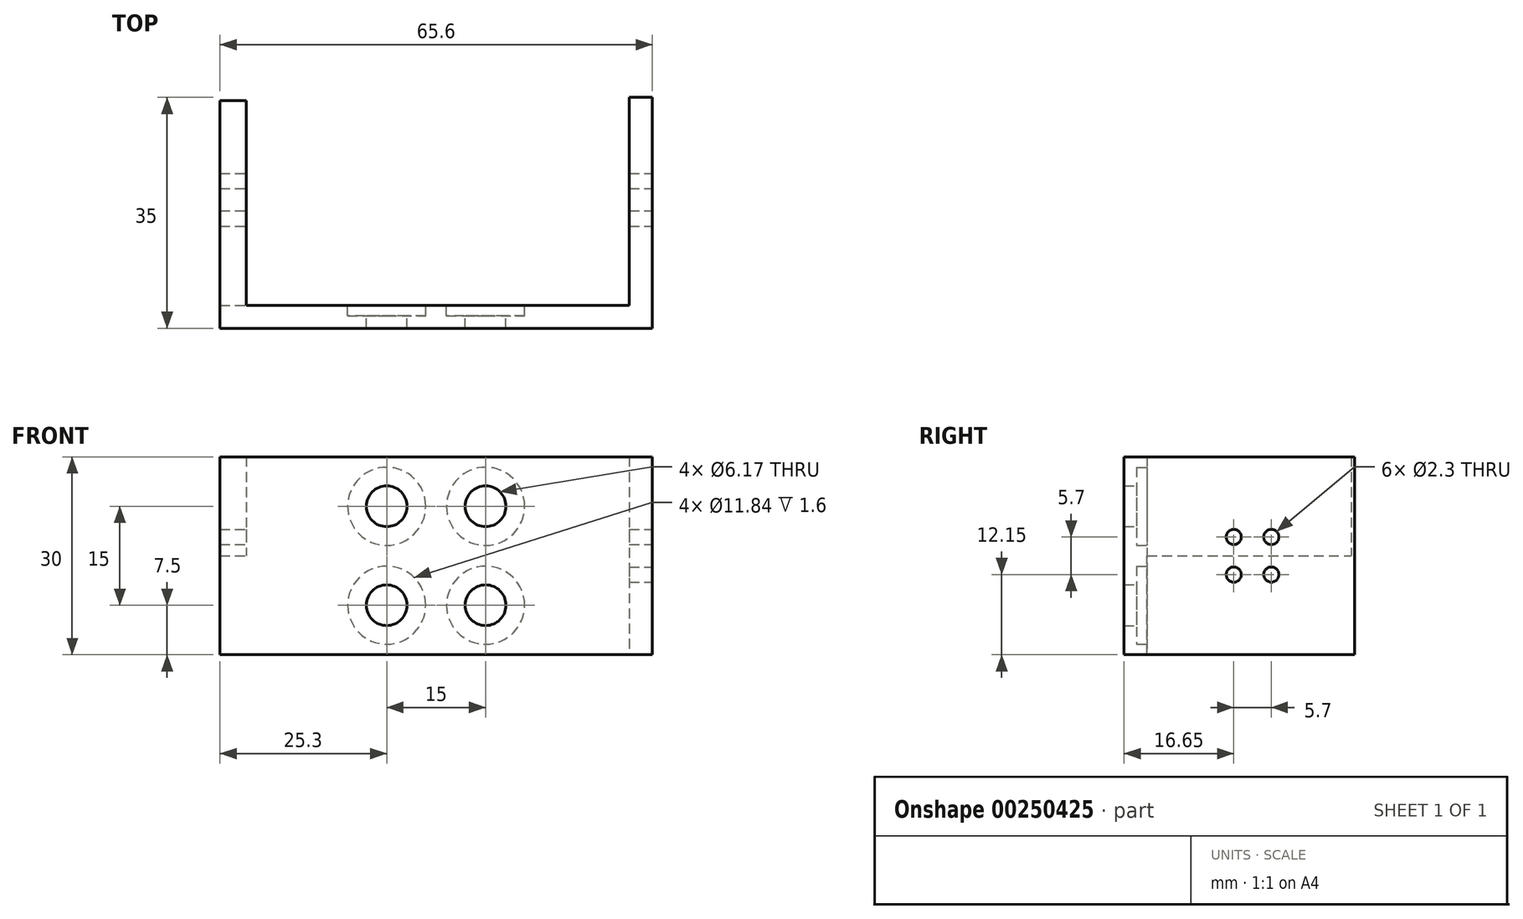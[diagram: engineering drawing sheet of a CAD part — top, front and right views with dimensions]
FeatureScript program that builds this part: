
annotation { "Feature Type Name" : "Feature", "Feature Type Description" : "" }
export const myFeature = defineFeature(function(context is Context, id is Id, definition is map)
    precondition{}
    {
        {
            var Q0;
            Q0=qCreatedBy(makeId("Front.planeOp"),FACE);
            var sketch = newSketch(context, id + "F0", { "sketchPlane" : qUnion([Q0])});
            skLineSegment(sketch, "E0.bottom", {"start": v(32.8, -15) * mm, "end": v(-32.8, -15) * mm});
            skLineSegment(sketch, "E0.top", {"start": v(32.8, 15) * mm, "end": v(-32.8, 15) * mm});
            skLineSegment(sketch, "E0.left", {"start": v(32.8, -15) * mm, "end": v(32.8, 15) * mm});
            skLineSegment(sketch, "E0.right", {"start": v(-32.8, -15) * mm, "end": v(-32.8, 15) * mm});
            skPoint(sketch, "E0.middle", {"position": v(0, 0) * mm});
            skSolve(sketch);
        }
        {
            var Q0;
            Q0 = qSketchRegion(id + "F0", true);
            extrude(context, id + "F1", {"entities" : qUnion([Q0]), "endBound" : BoundingType.SYMMETRIC, "depth" : 3.5 * mm});
        }
        {
            var Q0;
            Q0=qCreatedBy(makeId("Top.planeOp"),FACE);
            var sketch = newSketch(context, id + "F2", { "sketchPlane" : qUnion([Q0])});
            skLineSegment(sketch, "E1.bottom", {"start": v(32.8, 1.75) * mm, "end": v(29.3, 1.75) * mm});
            skLineSegment(sketch, "E1.top", {"start": v(32.8, 33.25) * mm, "end": v(29.3, 33.25) * mm});
            skLineSegment(sketch, "E1.left", {"start": v(32.8, 1.75) * mm, "end": v(32.8, 33.25) * mm});
            skLineSegment(sketch, "E1.right", {"start": v(29.3, 1.75) * mm, "end": v(29.3, 33.25) * mm});
            skSolve(sketch);
        }
        {
            var Q0;
            Q0 = qSketchRegion(id + "F2", true);
            extrude(context, id + "F3", {"entities" : qUnion([Q0]), "operationType" : NewBodyOperationType.ADD, "endBound" : BoundingType.SYMMETRIC, "depth" : 30 * mm});
        }
        {
            var Q0;
            Q0=qCreatedBy(makeId("Top.planeOp"),FACE);
            var sketch = newSketch(context, id + "F4", { "sketchPlane" : qUnion([Q0])});
            skLineSegment(sketch, "E2.bottom", {"start": v(-32.8, 1.75) * mm, "end": v(-28.8, 1.75) * mm});
            skLineSegment(sketch, "E2.top", {"start": v(-32.8, 32.75) * mm, "end": v(-28.8, 32.75) * mm});
            skLineSegment(sketch, "E2.left", {"start": v(-32.8, 1.75) * mm, "end": v(-32.8, 32.75) * mm});
            skLineSegment(sketch, "E2.right", {"start": v(-28.8, 1.75) * mm, "end": v(-28.8, 32.75) * mm});
            skSolve(sketch);
        }
        {
            var Q0;
            Q0 = qSketchRegion(id + "F4", true);
            extrude(context, id + "F5", {"entities" : qUnion([Q0]), "operationType" : NewBodyOperationType.ADD, "depth" : 15 * mm});
        }
        {
            var Q0;
            Q0=makeQuery(id+"F3.boolean.opBoolean","MERGE",FACE,{"derivedFrom":[makeQuery(id+"F1.opExtrude","SWEPT_FACE",FACE,{"disambiguationData":[OSD([sQuery(id+"F0.wireOp",EDGE,"E0.left")])]}),makeQuery(id+"F3.opExtrude","SWEPT_FACE",FACE,{"disambiguationData":[OSD([sQuery(id+"F2.wireOp",EDGE,"E1.left")])]})]});
            var sketch = newSketch(context, id + "F6", { "sketchPlane" : qUnion([Q0])});
            skCircle(sketch, "E3", {"center": v(14.9, 2.85) * mm, "radius": 1.15 * mm});
            skCircle(sketch, "E4", {"center": v(20.6, 2.85) * mm, "radius": 1.15 * mm});
            skCircle(sketch, "E5", {"center": v(14.9, -2.85) * mm, "radius": 1.15 * mm});
            skCircle(sketch, "E6", {"center": v(20.6, -2.85) * mm, "radius": 1.15 * mm});
            skLineSegment(sketch, "E7", {"start": v(14.9, 2.85) * mm, "end": v(14.9, -2.85) * mm, "construction": true});
            skLineSegment(sketch, "E8", {"start": v(14.9, -2.85) * mm, "end": v(20.6, -2.85) * mm, "construction": true});
            skLineSegment(sketch, "E9", {"start": v(20.6, -2.85) * mm, "end": v(20.6, 2.85) * mm, "construction": true});
            skLineSegment(sketch, "E10", {"start": v(20.6, 2.85) * mm, "end": v(14.9, 2.85) * mm, "construction": true});
            skSolve(sketch);
        }
        {
            var Q0;
            Q0 = qSketchRegion(id + "F6", true);
            extrude(context, id + "F7", {"entities" : qUnion([Q0]), "operationType" : NewBodyOperationType.REMOVE, "oppositeDirection" : true, "depth" : 200 * mm});
        }
        {
            var Q0;
            Q0=makeQuery(id+"F1.opExtrude","CAP_FACE",FACE,{"disambiguationData":[OSD([sQuery(id+"F0.wireOp",EDGE,"E0.bottom"),sQuery(id+"F0.wireOp",EDGE,"E0.top"),sQuery(id+"F0.wireOp",EDGE,"E0.left"),sQuery(id+"F0.wireOp",EDGE,"E0.right")])],"isStart":true});
            var sketch = newSketch(context, id + "F8", { "sketchPlane" : qUnion([Q0])});
            skCircle(sketch, "E11", {"center": v(-7.5, 7.5) * mm, "radius": 3.09 * mm});
            skCircle(sketch, "E12", {"center": v(-7.5, -7.5) * mm, "radius": 3.09 * mm});
            skCircle(sketch, "E13", {"center": v(7.5, 7.5) * mm, "radius": 3.09 * mm});
            skCircle(sketch, "E14", {"center": v(7.5, -7.5) * mm, "radius": 3.09 * mm});
            skLineSegment(sketch, "E15", {"start": v(-7.5, 7.5) * mm, "end": v(0, 7.5) * mm, "construction": true});
            skLineSegment(sketch, "E16", {"start": v(7.5, 7.5) * mm, "end": v(0, 7.5) * mm, "construction": true});
            skLineSegment(sketch, "E17", {"start": v(7.5, 7.5) * mm, "end": v(7.5, 0) * mm, "construction": true});
            skLineSegment(sketch, "E18", {"start": v(7.5, -7.5) * mm, "end": v(7.5, 0) * mm, "construction": true});
            skLineSegment(sketch, "E19", {"start": v(7.5, -7.5) * mm, "end": v(0, -7.5) * mm, "construction": true});
            skLineSegment(sketch, "E20", {"start": v(0, -7.5) * mm, "end": v(-7.5, -7.5) * mm, "construction": true});
            skLineSegment(sketch, "E21", {"start": v(-7.5, -7.5) * mm, "end": v(-7.5, 0) * mm, "construction": true});
            skLineSegment(sketch, "E22", {"start": v(-7.5, 0) * mm, "end": v(-7.5, 7.5) * mm, "construction": true});
            skSolve(sketch);
        }
        {
            var Q0;
            Q0 = qSketchRegion(id + "F8", true);
            extrude(context, id + "F9", {"entities" : qUnion([Q0]), "operationType" : NewBodyOperationType.REMOVE, "oppositeDirection" : true, "depth" : 25 * mm});
        }
        {
            var Q0;
            Q0=makeQuery(id+"F1.opExtrude","CAP_FACE",FACE,{"disambiguationData":[OSD([sQuery(id+"F0.wireOp",EDGE,"E0.bottom"),sQuery(id+"F0.wireOp",EDGE,"E0.top"),sQuery(id+"F0.wireOp",EDGE,"E0.left"),sQuery(id+"F0.wireOp",EDGE,"E0.right")])],"isStart":true});
            var sketch = newSketch(context, id + "F10", { "sketchPlane" : qUnion([Q0])});
            skCircle(sketch, "E23", {"center": v(-7.5, 7.5) * mm, "radius": 5.92 * mm});
            skCircle(sketch, "E24", {"center": v(-7.5, -7.5) * mm, "radius": 5.92 * mm});
            skCircle(sketch, "E25", {"center": v(7.5, -7.5) * mm, "radius": 5.92 * mm});
            skCircle(sketch, "E26", {"center": v(7.5, 7.5) * mm, "radius": 5.92 * mm});
            skSolve(sketch);
        }
        {
            var Q0;
            Q0 = qSketchRegion(id + "F10", true);
            extrude(context, id + "F11", {"entities" : qUnion([Q0]), "operationType" : NewBodyOperationType.REMOVE, "oppositeDirection" : true, "depth" : 1.6 * mm});
        }
    });
